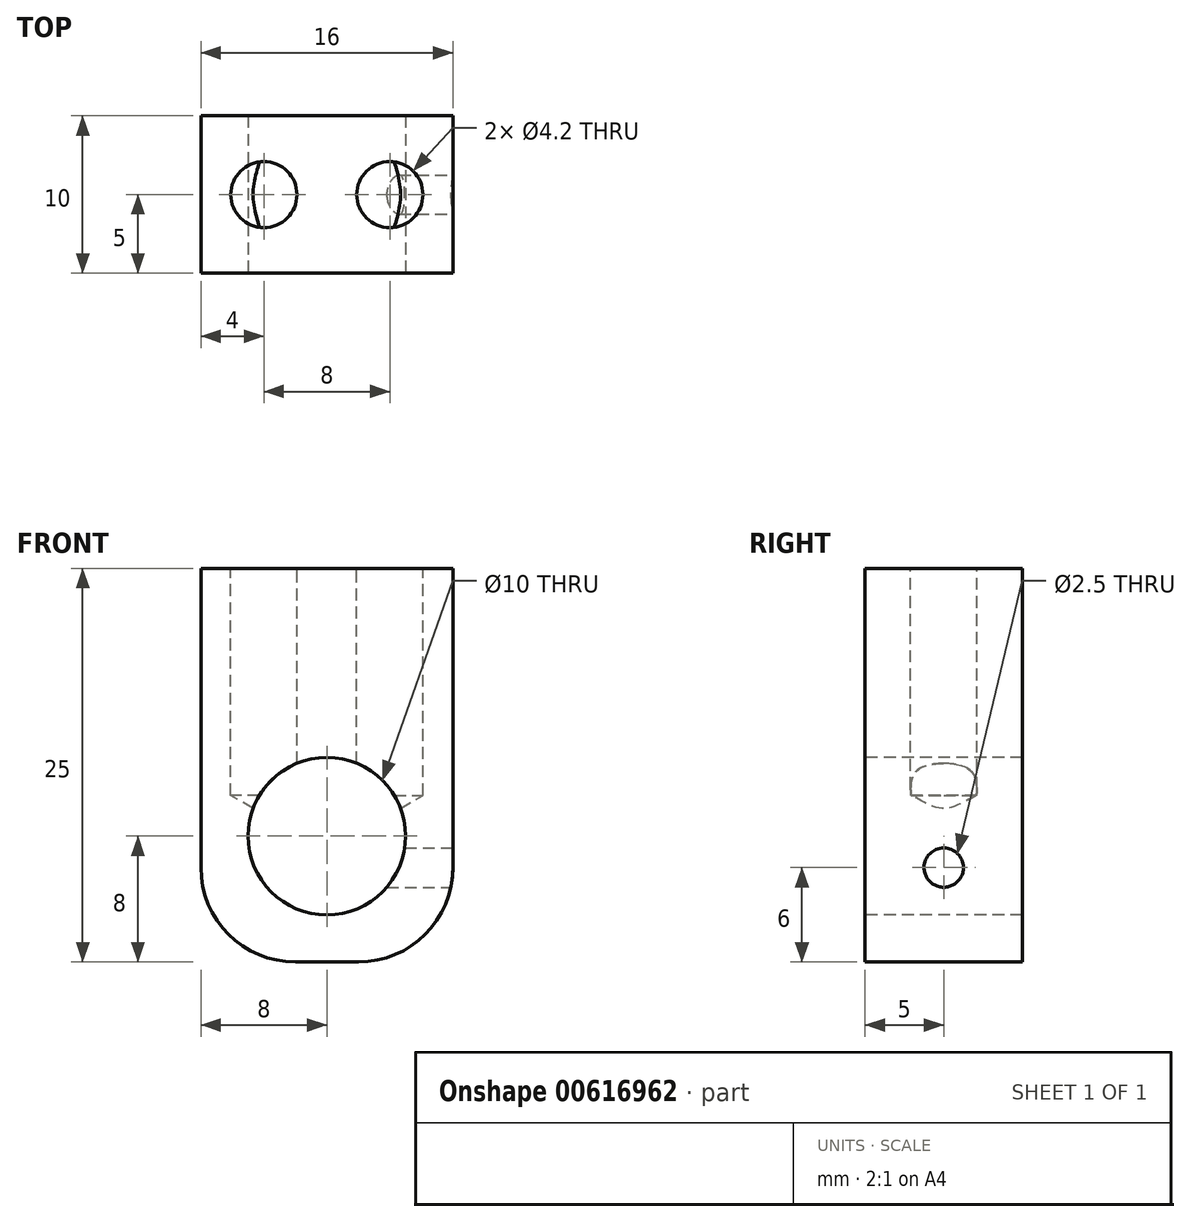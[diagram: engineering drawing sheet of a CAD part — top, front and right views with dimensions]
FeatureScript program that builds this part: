
annotation { "Feature Type Name" : "Feature", "Feature Type Description" : "" }
export const myFeature = defineFeature(function(context is Context, id is Id, definition is map)
    precondition{}
    {
        {
            var Q0;
            Q0=qCreatedBy(makeId("Front.planeOp"),FACE);
            var sketch = newSketch(context, id + "F0", { "sketchPlane" : qUnion([Q0])});
            skLineSegment(sketch, "E0.bottom", {"start": v(-8, 12.5) * mm, "end": v(8, 12.5) * mm});
            skLineSegment(sketch, "E0.top", {"start": v(-2, -12.5) * mm, "end": v(2, -12.5) * mm});
            skLineSegment(sketch, "E0.left", {"start": v(-8, 12.5) * mm, "end": v(-8, -6.5) * mm});
            skLineSegment(sketch, "E0.right", {"start": v(8, 12.5) * mm, "end": v(8, -6.5) * mm});
            skPoint(sketch, "E1", {"position": v(0, -4.5) * mm});
            skCircle(sketch, "E2", {"center": v(0, -4.5) * mm, "radius": 5 * mm});
            skPoint(sketch, "E3.visualSharp", {"position": v(8, -12.5) * mm});
            skArc(sketch, "E3.filletArc", {"start": v(2, -12.5) * mm, "mid": v(6.24, -10.74) * mm, "end": v(8, -6.5) * mm});
            skPoint(sketch, "E4.visualSharp", {"position": v(-8, -12.5) * mm});
            skArc(sketch, "E4.filletArc", {"start": v(-8, -6.5) * mm, "mid": v(-6.24, -10.74) * mm, "end": v(-2, -12.5) * mm});
            skSolve(sketch);
        }
        {
            var Q0;
            Q0=makeQuery(id+"F0.imprint","IMPRINT",FACE,{"disambiguationData":[TD([[makeQuery(id+"F0.imprint","IMPRINT",EDGE,{"derivedFrom":sQuery(id+"F0.wireOp",EDGE,"E0.bottom")}),-1.0]])]});
            extrude(context, id + "F1", {"entities" : qUnion([Q0]), "oppositeDirection" : true, "depth" : 10 * mm, "offsetDistance" : 25 * mm});
        }
        {
            var Q0;
            Q0=makeQuery(id+"F1.opExtrude","SWEPT_FACE",FACE,{"disambiguationData":[OSD([sQuery(id+"F0.wireOp",EDGE,"E0.bottom")])]});
            var sketch = newSketch(context, id + "F2", { "sketchPlane" : qUnion([Q0])});
            skPoint(sketch, "E5", {"position": v(-4, 5) * mm});
            skPoint(sketch, "E6", {"position": v(4, 5) * mm});
            skSolve(sketch);
        }
        {
            var Q0;
            Q0=sQuery(id+"F2.wireOp",VERTEX,"E5");
            var Q1;
            Q1=sQuery(id+"F2.wireOp",VERTEX,"E6");
            var Q2;
            Q2=makeQuery(id+"F1.opExtrude","SWEPT_BODY",BODY,{"disambiguationData":[OSD([sQuery(id+"F0.wireOp",EDGE,"E0.bottom"),sQuery(id+"F0.wireOp",EDGE,"E0.top"),sQuery(id+"F0.wireOp",EDGE,"E0.left"),sQuery(id+"F0.wireOp",EDGE,"E0.right"),sQuery(id+"F0.wireOp",EDGE,"E2"),sQuery(id+"F0.wireOp",EDGE,"E3.filletArc"),sQuery(id+"F0.wireOp",EDGE,"E4.filletArc")])]});
            hole(context, id + "F3", {"style" : HoleStyle.SIMPLE, "endStyle" : HoleEndStyle.BLIND, "standardTappedOrClearance" : lookupTablePath({ "standard" : "ISO", "engagement" : "75%", "pitch" : "0.8 mm", "size" : "M5", "type" : "Tapped" }), "standardBlindInLast" : lookupTablePath({ "standard" : "ISO", "engagement" : "75%", "pitch" : "0.8 mm", "size" : "M5", "type" : "Tapped" }), "holeDiameter" : 4.2 * mm, "majorDiameter" : 5 * mm, "showTappedDepth" : true, "holeDepth" : 14.4 * mm, "isTappedThrough" : true, "tappedDepth" : 12 * mm, "tapClearance" : 3, "locations" : qUnion([Q0, Q1]), "scope" : qUnion([Q2])});
        }
        {
            var Q0;
            Q0=makeQuery(id+"F1.opExtrude","SWEPT_FACE",FACE,{"disambiguationData":[OSD([sQuery(id+"F0.wireOp",EDGE,"E0.right")])]});
            var sketch = newSketch(context, id + "F4", { "sketchPlane" : qUnion([Q0])});
            skPoint(sketch, "E7", {"position": v(5, -6.5) * mm});
            skSolve(sketch);
        }
        {
            var Q0;
            Q0=sQuery(id+"F4.wireOp",VERTEX,"E7");
            var Q1;
            Q1=makeQuery(id+"F1.opExtrude","SWEPT_BODY",BODY,{"disambiguationData":[OSD([sQuery(id+"F0.wireOp",EDGE,"E0.bottom"),sQuery(id+"F0.wireOp",EDGE,"E0.top"),sQuery(id+"F0.wireOp",EDGE,"E0.left"),sQuery(id+"F0.wireOp",EDGE,"E0.right"),sQuery(id+"F0.wireOp",EDGE,"E2"),sQuery(id+"F0.wireOp",EDGE,"E3.filletArc"),sQuery(id+"F0.wireOp",EDGE,"E4.filletArc")])]});
            hole(context, id + "F5", {"style" : HoleStyle.SIMPLE, "endStyle" : HoleEndStyle.BLIND, "standardTappedOrClearance" : lookupTablePath({ "standard" : "ISO", "engagement" : "75%", "pitch" : "0.5 mm", "size" : "M3", "type" : "Tapped" }), "standardBlindInLast" : lookupTablePath({ "standard" : "ISO", "engagement" : "75%", "pitch" : "0.5 mm", "size" : "M3", "type" : "Tapped" }), "holeDiameter" : 2.5 * mm, "majorDiameter" : 3 * mm, "showTappedDepth" : true, "holeDepth" : 8 * mm, "isTappedThrough" : true, "tappedDepth" : 6.5 * mm, "tapClearance" : 3, "locations" : qUnion([Q0]), "scope" : qUnion([Q1])});
        }
    });
